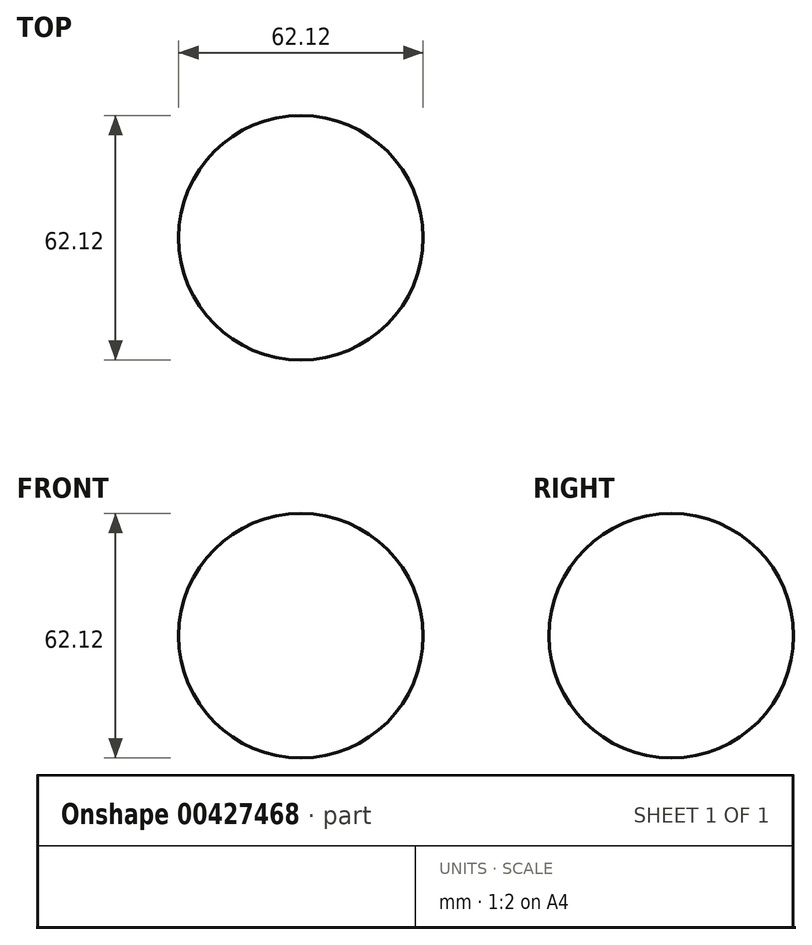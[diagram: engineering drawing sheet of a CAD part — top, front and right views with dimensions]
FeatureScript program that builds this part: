
annotation { "Feature Type Name" : "Feature", "Feature Type Description" : "" }
export const myFeature = defineFeature(function(context is Context, id is Id, definition is map)
    precondition{}
    {
        {
            var Q0;
            Q0=qCreatedBy(makeId("Front.planeOp"),FACE);
            var sketch = newSketch(context, id + "F0", { "sketchPlane" : qUnion([Q0])});
            skArc(sketch, "E0", {"start": v(0, -75.93) * mm, "mid": v(31.06, -44.87) * mm, "end": v(0, -13.8) * mm});
            skArc(sketch, "E1", {"start": v(0, -13.8) * mm, "mid": v(-22.6, 8.79) * mm, "end": v(0, 31.38) * mm});
            skArc(sketch, "E2", {"start": v(0, 31.38) * mm, "mid": v(-16.49, 47.86) * mm, "end": v(0, 64.35) * mm});
            skLineSegment(sketch, "E3", {"start": v(0, 64.35) * mm, "end": v(0, 31.38) * mm});
            skLineSegment(sketch, "E4", {"start": v(0, 31.38) * mm, "end": v(0, -13.8) * mm});
            skLineSegment(sketch, "E5", {"start": v(0, -13.8) * mm, "end": v(0, -75.93) * mm});
            skLineSegment(sketch, "E6", {"start": v(0, 70.91) * mm, "end": v(0, -75.93) * mm});
            skSolve(sketch);
        }
        {
            var Q0;
            {var subQ0=sQuery(id+"F0.wireOp",EDGE,"E2");Q0=makeQuery(id+"F0.imprint","IMPRINT",FACE,{"disambiguationData":[TD([[makeQuery(id+"F0.imprint","IMPRINT",EDGE,{"derivedFrom":subQ0}),-1.0]])]});}
            var Q1;
            {var subQ0=sQuery(id+"F0.wireOp",EDGE,"E1");Q1=makeQuery(id+"F0.imprint","IMPRINT",FACE,{"disambiguationData":[TD([[makeQuery(id+"F0.imprint","IMPRINT",EDGE,{"derivedFrom":subQ0}),-1.0]])]});}
            var Q2;
            {var subQ0=sQuery(id+"F0.wireOp",EDGE,"E0");Q2=makeQuery(id+"F0.imprint","IMPRINT",FACE,{"disambiguationData":[TD([[makeQuery(id+"F0.imprint","IMPRINT",EDGE,{"derivedFrom":subQ0}),1.0]])]});}
            var Q3;
            Q3=sQuery(id+"F0.wireOp",EDGE,"E6");
            revolve(context, id + "F1", {"entities" : qUnion([Q0, Q1, Q2]), "axis" : qUnion([Q3]), "revolveType" : RevolveType.FULL});
        }
    });
